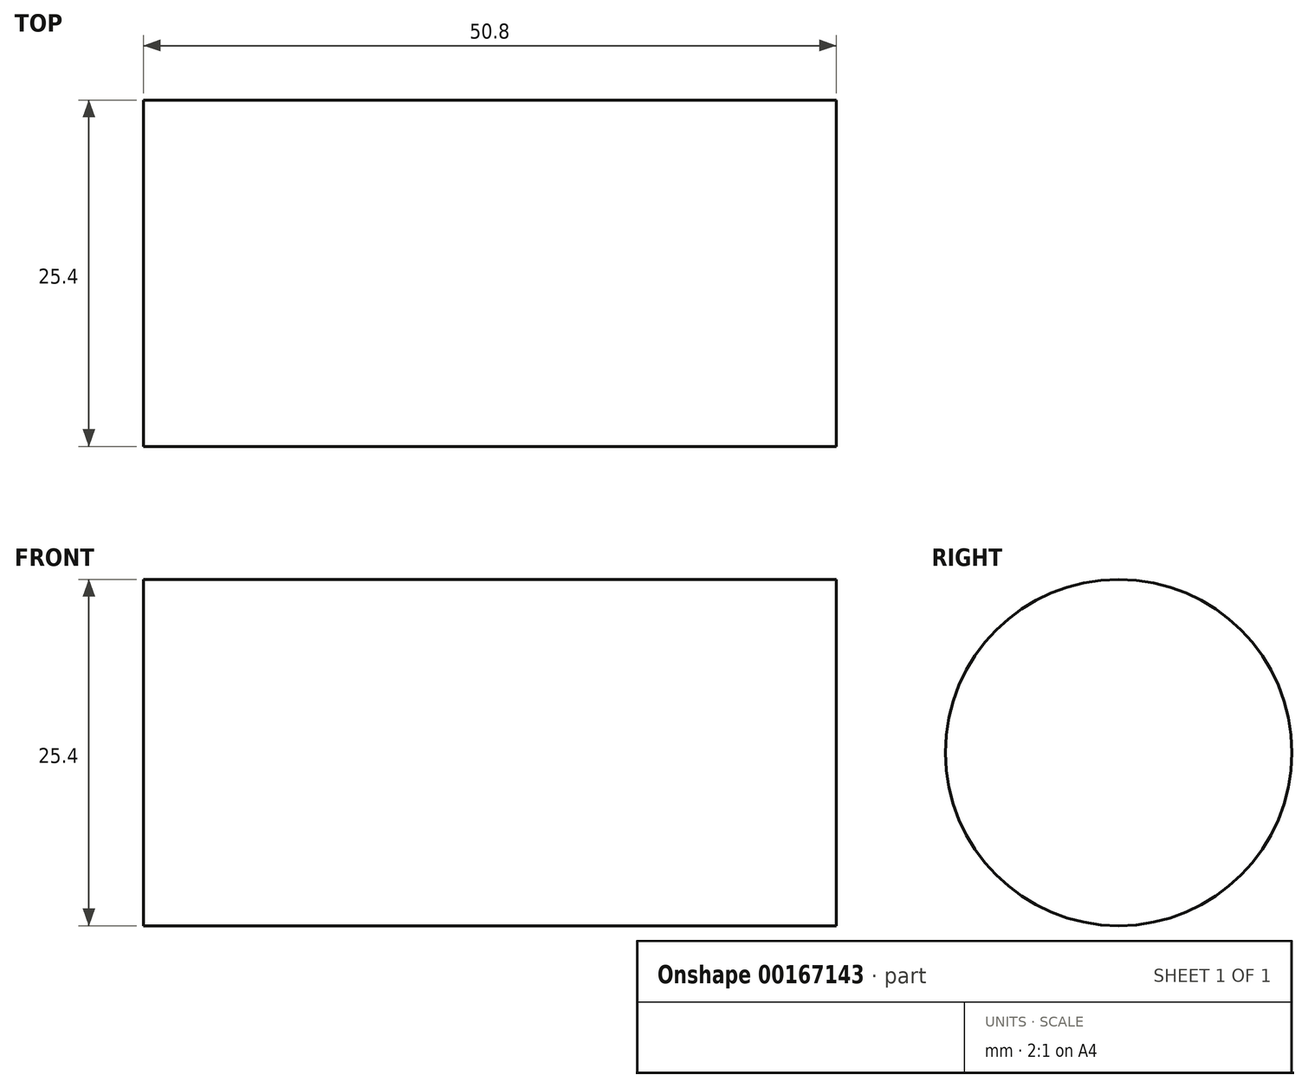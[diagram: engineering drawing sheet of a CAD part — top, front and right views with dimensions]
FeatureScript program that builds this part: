
annotation { "Feature Type Name" : "Feature", "Feature Type Description" : "" }
export const myFeature = defineFeature(function(context is Context, id is Id, definition is map)
    precondition{}
    {
        {
            var Q0;
            Q0=qCreatedBy(makeId("Right.planeOp"),FACE);
            var sketch = newSketch(context, id + "F0", { "sketchPlane" : qUnion([Q0])});
            skCircle(sketch, "E0", {"center": v(0, 0) * mm, "radius": 12.7 * mm});
            skSolve(sketch);
        }
        {
            var Q0;
            Q0 = qSketchRegion(id + "F0", true);
            extrude(context, id + "F1", {"entities" : qUnion([Q0]), "endBound" : BoundingType.SYMMETRIC, "depth" : 50.8 * mm});
        }
    });
